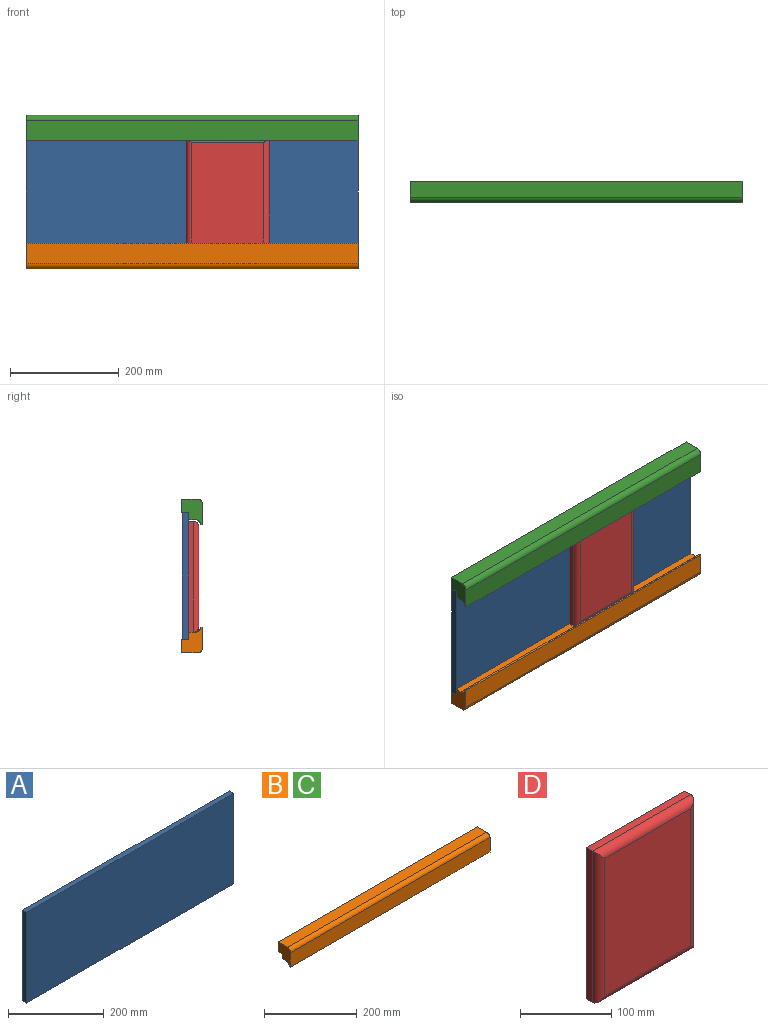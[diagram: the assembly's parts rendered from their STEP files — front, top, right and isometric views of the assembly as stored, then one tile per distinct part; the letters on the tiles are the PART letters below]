
ASSEMBLY  parts=4 mates=3
PART A: 6 faces, bbox 609.6x11.9x231.8 mm
  f0: plane 609.6x231.78mm, normal (0,-1,0), area 141290mm2, adj f1,f3,f4,f5
  f1: plane 609.6x11.91mm, normal (0,0,-1), area 7258mm2, adj f0,f2,f4,f5
  f2: plane 609.6x231.78mm, normal (0,1,0), area 141290mm2, adj f1,f3,f4,f5
  f3: plane 609.6x11.91mm, normal (0,0,1), area 7258mm2, adj f0,f2,f4,f5
  f4: plane 231.78x11.91mm, normal (1,0,0), area 2759.6mm2, adj f0,f1,f2,f3
  f5: plane 231.78x11.91mm, normal (-1,0,0), area 2759.6mm2, adj f0,f1,f2,f3
PART B: 11 faces, bbox 609.6x38.1x47.6 mm
  f0: plane 609.6x12.7mm, normal (0,0,-1), area 7741.9mm2, adj f1,f8,f9,f10
  f1: plane 609.6x25.4mm, normal (0,1,0), area 15483.8mm2, adj f0,f2,f9,f10
  f2: plane 609.6x28.58mm, normal (0,0,1), area 17419.3mm2, adj f1,f3,f9,f10
  f3: cylinder r=9.53mm len=609.6mm, axis (-1,0,0), area 9120.7mm2, adj f2,f4,f9,f10
  f4: plane 609.6x38.1mm, normal (0,-1,0), area 23225.8mm2, adj f3,f5,f9,f10
  f5: plane 609.6x3.18mm, normal (0,0,-1), area 1935.5mm2, adj f4,f6,f9,f10
  f6: cylinder r=9.53mm len=609.6mm, axis (-1,0,0), area 9120.7mm2, adj f5,f7,f9,f10
  f7: plane 609.6x12.7mm, normal (0,0,-1), area 7741.9mm2, adj f6,f8,f9,f10
  f8: plane 609.6x12.7mm, normal (0,1,0), area 7741.9mm2, adj f0,f7,f9,f10
  f9: plane 47.63x38.1mm, normal (1,0,0), area 1320.6mm2, adj f0,f1,f2,f3,f4,f5,f6,f7
  f10: plane 47.63x38.1mm, normal (-1,0,0), area 1320.6mm2, adj f0,f1,f2,f3,f4,f5,f6,f7
PART C: same geometry as B
PART D: 10 faces, bbox 152.4x19.1x203.2 mm
  f0: plane 152.4x9.53mm, normal (0,0,1), area 1451.6mm2, adj f1,f3,f5,f6
  f1: plane 203.2x9.53mm, normal (-1,0,0), area 1935.5mm2, adj f0,f2,f5,f7
  f2: plane 152.4x9.53mm, normal (0,0,-1), area 1451.6mm2, adj f1,f3,f5,f9
  f3: plane 203.2x9.53mm, normal (1,0,0), area 1935.5mm2, adj f0,f2,f5,f8
  f4: plane 184.15x133.35mm, normal (0,-1,0), area 24556.4mm2, adj f6,f7,f8,f9
  f5: plane 203.2x152.4mm, normal (0,1,0), area 30967.7mm2, adj f0,f1,f2,f3
  f6: cylinder r=9.53mm len=152.4mm, axis (1,0,0), area 2176.6mm2, adj f0,f4,f7,f8
  f7: cylinder r=9.53mm len=203.2mm, axis (0,0,1), area 2936.7mm2, adj f1,f4,f6,f9
  f8: cylinder r=9.53mm len=203.2mm, axis (0,0,-1), area 2936.7mm2, adj f3,f4,f6,f9
  f9: cylinder r=9.53mm len=152.4mm, axis (-1,0,0), area 2176.6mm2, adj f2,f4,f7,f8
PLACE A t=(-1757.42,-37.06,7.84)mm fixed
PLACE B rot(axis=(0,1,0),180deg) t=(-1147.82,4.76,-99.71)mm
PLACE C t=(-1757.42,4.76,87.61)mm
PLACE D t=(-1359.06,30.16,-41.15)mm
MATE slider B.f10 <-> D.f3  axis (1,0,0) through (-1147.82,30.16,-109.24)mm
MATE fastened B.f10 <-> A.f4  axis (1,0,0) through (-1147.82,30.16,-121.94)mm
MATE fastened C.f9 <-> A.f4  axis (1,0,0) through (-1147.82,30.16,109.84)mm
